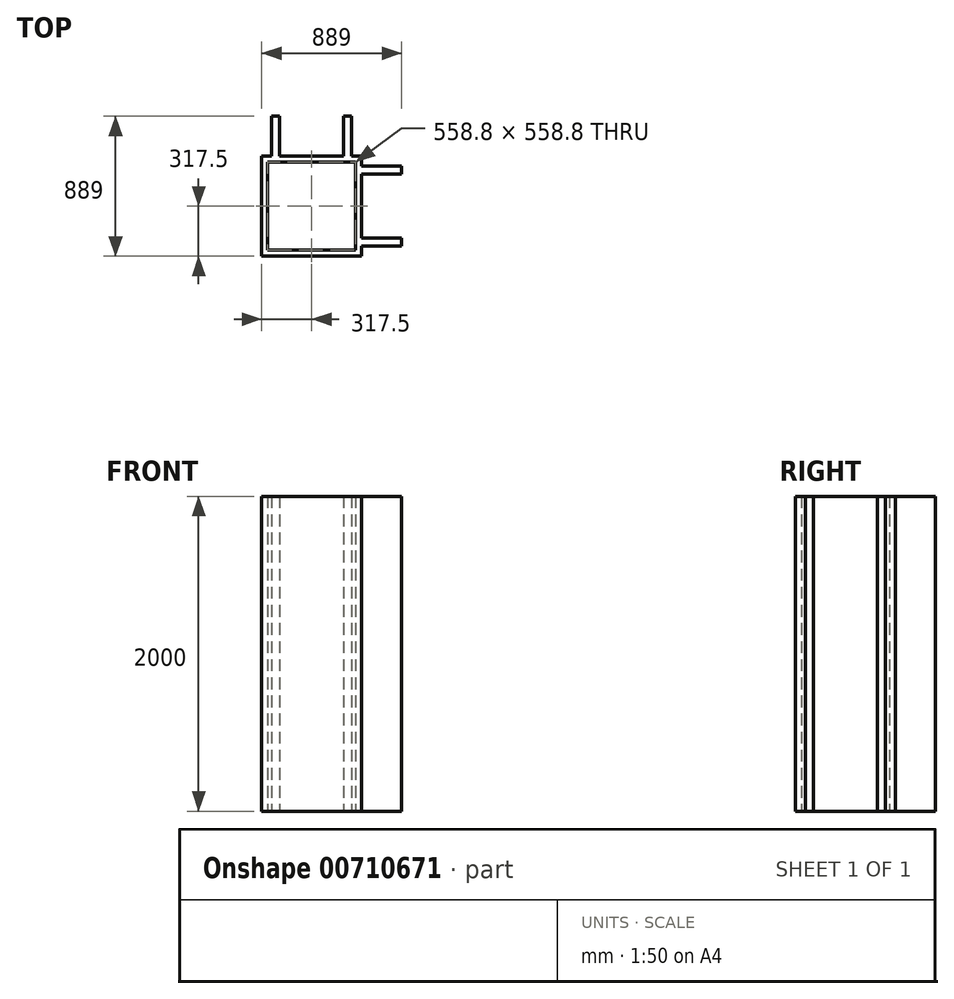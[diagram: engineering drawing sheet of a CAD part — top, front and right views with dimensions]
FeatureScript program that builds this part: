
annotation { "Feature Type Name" : "Feature", "Feature Type Description" : "" }
export const myFeature = defineFeature(function(context is Context, id is Id, definition is map)
    precondition{}
    {
        {
            var Q0;
            Q0=qCreatedBy(makeId("Top.planeOp"),FACE);
            var sketch = newSketch(context, id + "F0", { "sketchPlane" : qUnion([Q0])});
            skLineSegment(sketch, "E0.bottom", {"start": v(317.5, -317.5) * mm, "end": v(-317.5, -317.5) * mm});
            skLineSegment(sketch, "E0.top", {"start": v(317.5, 317.5) * mm, "end": v(-317.5, 317.5) * mm});
            skLineSegment(sketch, "E0.left", {"start": v(317.5, -317.5) * mm, "end": v(317.5, 317.5) * mm});
            skLineSegment(sketch, "E0.right", {"start": v(-317.5, -317.5) * mm, "end": v(-317.5, 317.5) * mm});
            skPoint(sketch, "E0.middle", {"position": v(0, 0) * mm});
            skLineSegment(sketch, "E1.bottom", {"start": v(279.4, -279.4) * mm, "end": v(-279.4, -279.4) * mm});
            skLineSegment(sketch, "E1.top", {"start": v(279.4, 279.4) * mm, "end": v(-279.4, 279.4) * mm});
            skLineSegment(sketch, "E1.left", {"start": v(279.4, -279.4) * mm, "end": v(279.4, 279.4) * mm});
            skLineSegment(sketch, "E1.right", {"start": v(-279.4, -279.4) * mm, "end": v(-279.4, 279.4) * mm});
            skSolve(sketch);
        }
        {
            var Q0;
            Q0=makeQuery(id+"F0.imprint","IMPRINT",FACE,{"disambiguationData":[TD([[makeQuery(id+"F0.imprint","IMPRINT",EDGE,{"derivedFrom":sQuery(id+"F0.wireOp",EDGE,"E0.bottom")}),-1.0]])]});
            extrude(context, id + "F1", {"entities" : qUnion([Q0]), "depth" : 2000 * mm, "offsetDistance" : 25.4 * mm});
        }
        {
            var Q0;
            Q0=qCreatedBy(makeId("Top.planeOp"),FACE);
            var sketch = newSketch(context, id + "F2", { "sketchPlane" : qUnion([Q0])});
            skLineSegment(sketch, "E2.bottom", {"start": v(203.2, 571.5) * mm, "end": v(254, 571.5) * mm});
            skLineSegment(sketch, "E2.top", {"start": v(203.2, 317.5) * mm, "end": v(254, 317.5) * mm});
            skLineSegment(sketch, "E2.left", {"start": v(203.2, 571.5) * mm, "end": v(203.2, 317.5) * mm});
            skLineSegment(sketch, "E2.right", {"start": v(254, 571.5) * mm, "end": v(254, 317.5) * mm});
            skLineSegment(sketch, "E3.bottom", {"start": v(-254, 571.5) * mm, "end": v(-203.2, 571.5) * mm});
            skLineSegment(sketch, "E3.top", {"start": v(-254, 317.5) * mm, "end": v(-203.2, 317.5) * mm});
            skLineSegment(sketch, "E3.left", {"start": v(-254, 571.5) * mm, "end": v(-254, 317.5) * mm});
            skLineSegment(sketch, "E3.right", {"start": v(-203.2, 571.5) * mm, "end": v(-203.2, 317.5) * mm});
            skLineSegment(sketch, "E4.bottom", {"start": v(317.5, -203.2) * mm, "end": v(571.5, -203.2) * mm});
            skLineSegment(sketch, "E4.top", {"start": v(317.5, -254) * mm, "end": v(571.5, -254) * mm});
            skLineSegment(sketch, "E4.left", {"start": v(317.5, -203.2) * mm, "end": v(317.5, -254) * mm});
            skLineSegment(sketch, "E4.right", {"start": v(571.5, -203.2) * mm, "end": v(571.5, -254) * mm});
            skLineSegment(sketch, "E5.bottom", {"start": v(317.5, 254) * mm, "end": v(571.5, 254) * mm});
            skLineSegment(sketch, "E5.top", {"start": v(317.5, 203.2) * mm, "end": v(571.5, 203.2) * mm});
            skLineSegment(sketch, "E5.left", {"start": v(317.5, 254) * mm, "end": v(317.5, 203.2) * mm});
            skLineSegment(sketch, "E5.right", {"start": v(571.5, 254) * mm, "end": v(571.5, 203.2) * mm});
            skSolve(sketch);
        }
        {
            var Q0;
            Q0=makeQuery(id+"F2.imprint","IMPRINT",FACE,{"disambiguationData":[TD([[makeQuery(id+"F2.imprint","IMPRINT",EDGE,{"derivedFrom":sQuery(id+"F2.wireOp",EDGE,"E3.bottom")}),-1.0]])]});
            var Q1;
            Q1=makeQuery(id+"F2.imprint","IMPRINT",FACE,{"disambiguationData":[TD([[makeQuery(id+"F2.imprint","IMPRINT",EDGE,{"derivedFrom":sQuery(id+"F2.wireOp",EDGE,"E2.bottom")}),-1.0]])]});
            var Q2;
            Q2=makeQuery(id+"F2.imprint","IMPRINT",FACE,{"disambiguationData":[TD([[makeQuery(id+"F2.imprint","IMPRINT",EDGE,{"derivedFrom":sQuery(id+"F2.wireOp",EDGE,"E5.bottom")}),-1.0]])]});
            var Q3;
            Q3=makeQuery(id+"F2.imprint","IMPRINT",FACE,{"disambiguationData":[TD([[makeQuery(id+"F2.imprint","IMPRINT",EDGE,{"derivedFrom":sQuery(id+"F2.wireOp",EDGE,"E4.bottom")}),-1.0]])]});
            var Q4;
            Q4=makeQuery(id+"F1.opExtrude","CAP_FACE",FACE,{"disambiguationData":[OSD([sQuery(id+"F0.wireOp",EDGE,"E0.bottom"),sQuery(id+"F0.wireOp",EDGE,"E0.top"),sQuery(id+"F0.wireOp",EDGE,"E0.left"),sQuery(id+"F0.wireOp",EDGE,"E0.right"),sQuery(id+"F0.wireOp",EDGE,"E1.bottom"),sQuery(id+"F0.wireOp",EDGE,"E1.top"),sQuery(id+"F0.wireOp",EDGE,"E1.left"),sQuery(id+"F0.wireOp",EDGE,"E1.right")])],"isStart":false});
            extrude(context, id + "F3", {"entities" : qUnion([Q0, Q1, Q2, Q3]), "operationType" : NewBodyOperationType.ADD, "endBound" : BoundingType.UP_TO_SURFACE, "depth" : 25.4 * mm, "endBoundEntityFace" : qUnion([Q4]), "offsetDistance" : 25.4 * mm});
        }
    });
